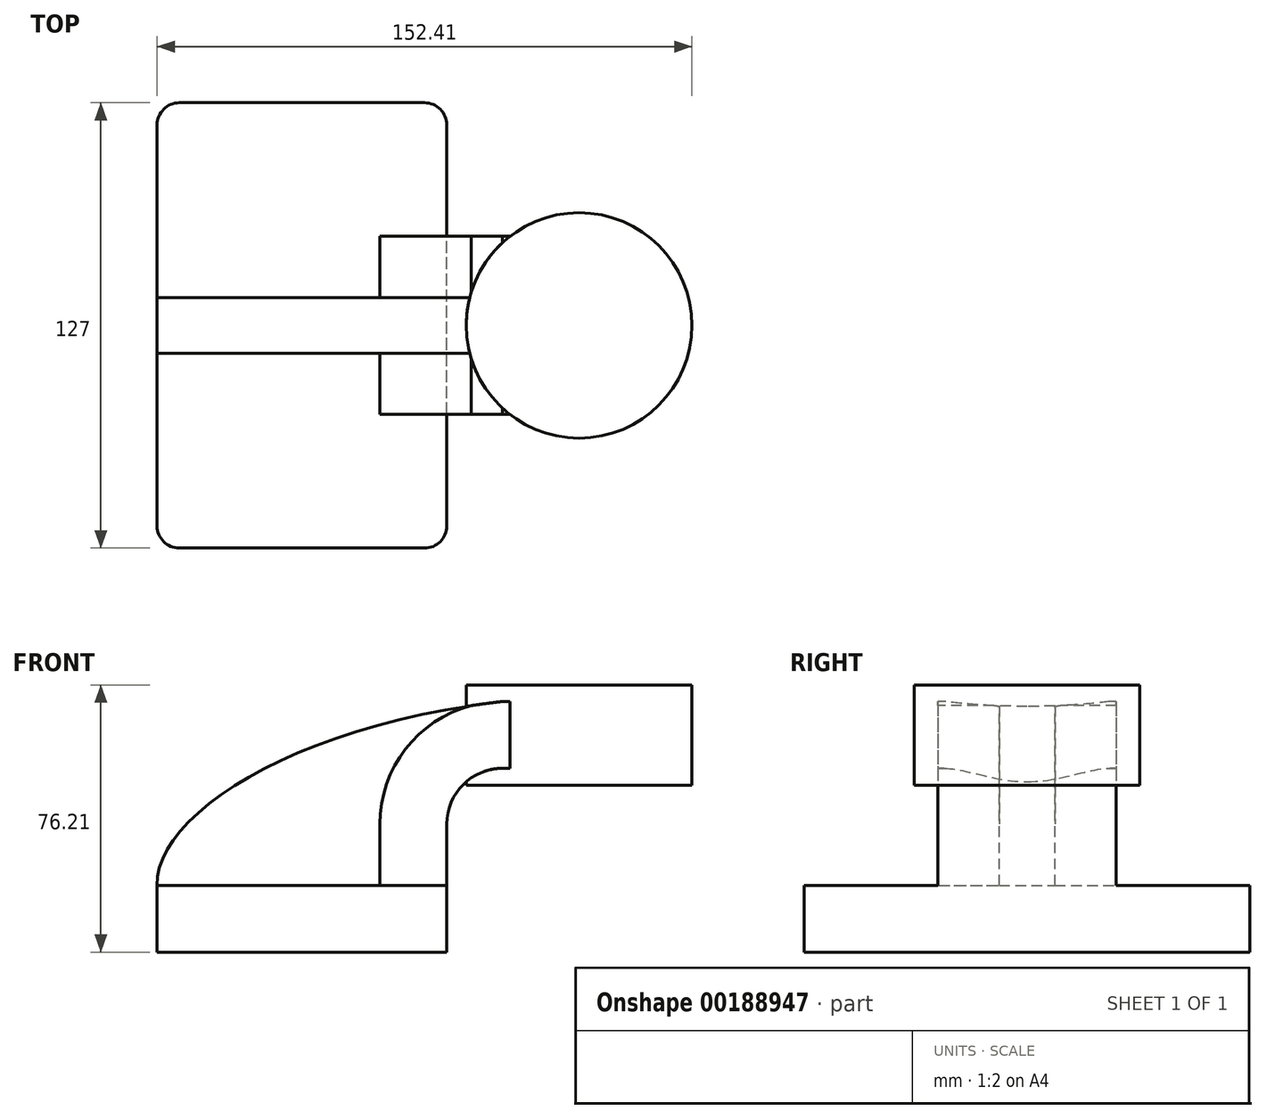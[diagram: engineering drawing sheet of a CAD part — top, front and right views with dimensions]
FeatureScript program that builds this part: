
annotation { "Feature Type Name" : "Feature", "Feature Type Description" : "" }
export const myFeature = defineFeature(function(context is Context, id is Id, definition is map)
    precondition{}
    {
        {
            var Q0;
            Q0=qCreatedBy(makeId("Front.planeOp"),FACE);
            var sketch = newSketch(context, id + "F0", { "sketchPlane" : qUnion([Q0])});
            skLineSegment(sketch, "E0.bottom", {"start": v(41.28, -9.52) * mm, "end": v(-41.28, -9.53) * mm});
            skLineSegment(sketch, "E0.top", {"start": v(41.28, 9.53) * mm, "end": v(-41.28, 9.52) * mm});
            skLineSegment(sketch, "E0.left", {"start": v(41.28, -9.52) * mm, "end": v(41.28, 9.53) * mm});
            skLineSegment(sketch, "E0.right", {"start": v(-41.28, -9.53) * mm, "end": v(-41.28, 9.52) * mm});
            skPoint(sketch, "E0.middle", {"position": v(0, 0) * mm});
            skLineSegment(sketch, "E1.bottom", {"start": v(111.12, 38.1) * mm, "end": v(60.32, 38.1) * mm});
            skLineSegment(sketch, "E1.top", {"start": v(111.12, 66.68) * mm, "end": v(60.32, 66.68) * mm});
            skLineSegment(sketch, "E1.left", {"start": v(111.12, 38.1) * mm, "end": v(111.12, 66.68) * mm});
            skLineSegment(sketch, "E1.right", {"start": v(60.32, 38.1) * mm, "end": v(60.32, 66.68) * mm});
            skPoint(sketch, "E1.middle", {"position": v(85.72, 52.39) * mm});
            skLineSegment(sketch, "E2", {"start": v(41.28, 9.53) * mm, "end": v(41.28, 27) * mm});
            skArc(sketch, "E3", {"start": v(41.28, 27) * mm, "mid": v(45.92, 38.23) * mm, "end": v(57.15, 42.88) * mm});
            skLineSegment(sketch, "E4", {"start": v(57.15, 42.88) * mm, "end": v(78.98, 42.88) * mm});
            skLineSegment(sketch, "E5.0", {"start": v(57.15, 61.93) * mm, "end": v(78.98, 61.93) * mm});
            skArc(sketch, "E5.1", {"start": v(22.23, 27) * mm, "mid": v(32.45, 51.7) * mm, "end": v(57.15, 61.93) * mm});
            skLineSegment(sketch, "E5.2", {"start": v(22.23, 9.53) * mm, "end": v(22.23, 27) * mm});
            skLineSegment(sketch, "E6", {"start": v(78.98, 38.1) * mm, "end": v(78.98, 66.68) * mm});
            skFitSpline(sketch, "E7", {"points": [v(-41.28, 9.52) * mm, v(57.15, 61.93) * mm], "startDerivative": vector(-1.81, 59.55) * mm, "endDerivative": vector(177.84, 19.77) * mm});
            skSolve(sketch);
        }
        {
            var Q0;
            Q0=makeQuery(id+"F0.imprint","IMPRINT",FACE,{"disambiguationData":[TD([[makeQuery(id+"F0.imprint","IMPRINT",EDGE,{"derivedFrom":sQuery(id+"F0.wireOp",EDGE,"E0.bottom")}),-1.0]])]});
            extrude(context, id + "F1", {"entities" : qUnion([Q0]), "endBound" : BoundingType.SYMMETRIC, "depth" : 127 * mm});
        }
        {
            var Q0;
            {var subQ1=sQuery(id+"F0.wireOp",EDGE,"E2");Q0=makeQuery(id+"F0.imprint","IMPRINT",FACE,{"disambiguationData":[TD([[makeQuery(id+"F0.imprint","IMPRINT",EDGE,{"derivedFrom":subQ1}),1.0]])]});}
            var Q1;
            {var subQ0=sQuery(id+"F0.wireOp",EDGE,"E4");var subQ1=sQuery(id+"F0.wireOp",EDGE,"E1.right");var subQ2=makeQuery(id+"F0.imprint","INTERSECT",VERTEX,{"derivedFrom":[subQ1,subQ0]});Q1=makeQuery(id+"F0.imprint","IMPRINT",FACE,{"disambiguationData":[TD([[makeQuery(id+"F0.imprint","IMPRINT",EDGE,{"disambiguationData":[TD([[subQ2,-1.0]])],"derivedFrom":subQ1}),-1.0]])]});}
            extrude(context, id + "F2", {"entities" : qUnion([Q0, Q1]), "operationType" : NewBodyOperationType.ADD, "endBound" : BoundingType.SYMMETRIC, "depth" : 50.8 * mm});
        }
        {
            var Q0;
            {var subQ3=sQuery(id+"F0.wireOp",EDGE,"E5.2");Q0=makeQuery(id+"F0.imprint","IMPRINT",FACE,{"disambiguationData":[TD([[makeQuery(id+"F0.imprint","IMPRINT",EDGE,{"derivedFrom":subQ3}),1.0]])]});}
            extrude(context, id + "F3", {"entities" : qUnion([Q0]), "operationType" : NewBodyOperationType.ADD, "endBound" : BoundingType.SYMMETRIC, "depth" : 15.88 * mm});
        }
        {
            var Q0;
            {var subQ0=sQuery(id+"F0.wireOp",EDGE,"E1.left");Q0=makeQuery(id+"F0.imprint","IMPRINT",FACE,{"disambiguationData":[TD([[makeQuery(id+"F0.imprint","IMPRINT",EDGE,{"derivedFrom":subQ0}),1.0]])]});}
            var Q1;
            Q1=sQuery(id+"F0.wireOp",EDGE,"E6");
            revolve(context, id + "F4", {"operationType" : NewBodyOperationType.ADD, "entities" : qUnion([Q0]), "axis" : qUnion([Q1]), "revolveType" : RevolveType.FULL});
        }
        {
            var Q0;
            Q0=makeQuery(id+"F1.opExtrude","CAP_EDGE",EDGE,{"disambiguationData":[OSD([sQuery(id+"F0.wireOp",EDGE,"E0.right")])],"isStart":false});
            var Q1;
            Q1=makeQuery(id+"F1.opExtrude","CAP_EDGE",EDGE,{"disambiguationData":[OSD([sQuery(id+"F0.wireOp",EDGE,"E0.right")])],"isStart":true});
            var Q2;
            Q2=makeQuery(id+"F1.opExtrude","CAP_EDGE",EDGE,{"disambiguationData":[OSD([sQuery(id+"F0.wireOp",EDGE,"E0.left")])],"isStart":false});
            var Q3;
            Q3=makeQuery(id+"F1.opExtrude","CAP_EDGE",EDGE,{"disambiguationData":[OSD([sQuery(id+"F0.wireOp",EDGE,"E0.left")])],"isStart":true});
            fillet(context, id + "F5", {"entities" : qUnion([Q0, Q1, Q2, Q3]), "radius" : 6.35 * mm, "tangentPropagation" : true, "allowEdgeOverflow" : false});
        }
    });
